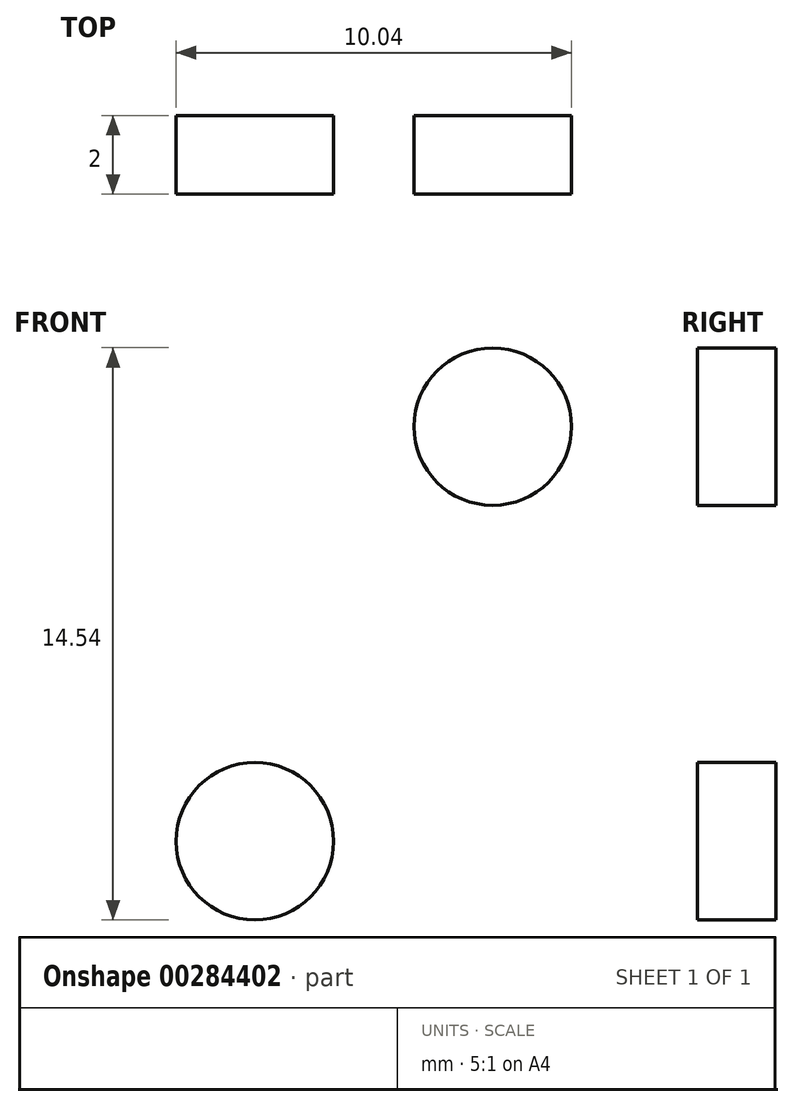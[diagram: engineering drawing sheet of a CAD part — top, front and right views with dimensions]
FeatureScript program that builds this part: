
annotation { "Feature Type Name" : "Feature", "Feature Type Description" : "" }
export const myFeature = defineFeature(function(context is Context, id is Id, definition is map)
    precondition{}
    {
        {
            var Q0;
            Q0=qCreatedBy(makeId("Front.planeOp"),FACE);
            var sketch = newSketch(context, id + "F0", { "sketchPlane" : qUnion([Q0])});
            skCircle(sketch, "E0", {"center": v(0, 0) * mm, "radius": 10 * mm});
            skSolve(sketch);
        }
        {
            var Q0;
            Q0=makeQuery(id+"F0.imprint","IMPRINT",FACE,{"disambiguationData":[TD([[makeQuery(id+"F0.imprint","IMPRINT",EDGE,{"derivedFrom":sQuery(id+"F0.wireOp",EDGE,"E0")}),1.0]])]});
            extrude(context, id + "F1", {"entities" : qUnion([Q0]), "depth" : 2 * mm});
        }
        {
            var Q0;
            Q0=makeQuery(id+"F1.opExtrude","CAP_FACE",FACE,{"disambiguationData":[OSD([sQuery(id+"F0.wireOp",EDGE,"E0")])],"isStart":false});
            var sketch = newSketch(context, id + "F2", { "sketchPlane" : qUnion([Q0])});
            skCircle(sketch, "E1", {"center": v(0, 0) * mm, "radius": 7 * mm});
            skCircle(sketch, "E2", {"center": v(0, 7) * mm, "radius": 2 * mm});
            skCircle(sketch, "E3", {"center": v(6.04, 3.54) * mm, "radius": 2 * mm});
            skCircle(sketch, "E4", {"center": v(5.81, -3.9) * mm, "radius": 2 * mm});
            skCircle(sketch, "E5", {"center": v(0, -7) * mm, "radius": 2 * mm});
            skCircle(sketch, "E6", {"center": v(-6.31, -3.03) * mm, "radius": 2 * mm});
            skCircle(sketch, "E7", {"center": v(-5.68, 4.1) * mm, "radius": 2 * mm});
            skSolve(sketch);
        }
        {
            var Q0;
            {var subQ0=sQuery(id+"F2.wireOp",EDGE,"E7");var subQ1=sQuery(id+"F2.wireOp",EDGE,"E1");var subQ2=makeQuery(id+"F2.imprint","INTERSECT",VERTEX,{"disambiguationData":[OD(0.0)],"derivedFrom":[subQ1,subQ0]});Q0=makeQuery(id+"F2.imprint","IMPRINT",FACE,{"disambiguationData":[TD([[makeQuery(id+"F2.imprint","IMPRINT",EDGE,{"disambiguationData":[TD([[subQ2,-1.0]])],"derivedFrom":subQ1}),-1.0]])]});}
            var Q1;
            {var subQ0=sQuery(id+"F2.wireOp",EDGE,"E7");var subQ1=sQuery(id+"F2.wireOp",EDGE,"E1");var subQ2=makeQuery(id+"F2.imprint","INTERSECT",VERTEX,{"disambiguationData":[OD(0.0)],"derivedFrom":[subQ1,subQ0]});Q1=makeQuery(id+"F2.imprint","IMPRINT",FACE,{"disambiguationData":[TD([[makeQuery(id+"F2.imprint","IMPRINT",EDGE,{"disambiguationData":[TD([[subQ2,-1.0]])],"derivedFrom":subQ1}),1.0]])]});}
            var Q2;
            {var subQ0=sQuery(id+"F2.wireOp",EDGE,"E2");var subQ1=sQuery(id+"F2.wireOp",EDGE,"E1");var subQ2=makeQuery(id+"F2.imprint","INTERSECT",VERTEX,{"disambiguationData":[OD(0.0)],"derivedFrom":[subQ1,subQ0]});Q2=makeQuery(id+"F2.imprint","IMPRINT",FACE,{"disambiguationData":[TD([[makeQuery(id+"F2.imprint","IMPRINT",EDGE,{"disambiguationData":[TD([[subQ2,-1.0]])],"derivedFrom":subQ1}),1.0]])]});}
            var Q3;
            {var subQ0=sQuery(id+"F2.wireOp",EDGE,"E2");var subQ1=sQuery(id+"F2.wireOp",EDGE,"E1");var subQ2=makeQuery(id+"F2.imprint","INTERSECT",VERTEX,{"disambiguationData":[OD(0.0)],"derivedFrom":[subQ1,subQ0]});Q3=makeQuery(id+"F2.imprint","IMPRINT",FACE,{"disambiguationData":[TD([[makeQuery(id+"F2.imprint","IMPRINT",EDGE,{"disambiguationData":[TD([[subQ2,-1.0]])],"derivedFrom":subQ1}),-1.0]])]});}
            var Q4;
            {var subQ0=sQuery(id+"F2.wireOp",EDGE,"E3");var subQ1=sQuery(id+"F2.wireOp",EDGE,"E1");var subQ2=makeQuery(id+"F2.imprint","INTERSECT",VERTEX,{"disambiguationData":[OD(0.0)],"derivedFrom":[subQ1,subQ0]});Q4=makeQuery(id+"F2.imprint","IMPRINT",FACE,{"disambiguationData":[TD([[makeQuery(id+"F2.imprint","IMPRINT",EDGE,{"disambiguationData":[TD([[subQ2,1.0]])],"derivedFrom":subQ1}),-1.0]])]});}
            var Q5;
            {var subQ0=sQuery(id+"F2.wireOp",EDGE,"E3");var subQ1=sQuery(id+"F2.wireOp",EDGE,"E1");var subQ2=makeQuery(id+"F2.imprint","INTERSECT",VERTEX,{"disambiguationData":[OD(0.0)],"derivedFrom":[subQ1,subQ0]});Q5=makeQuery(id+"F2.imprint","IMPRINT",FACE,{"disambiguationData":[TD([[makeQuery(id+"F2.imprint","IMPRINT",EDGE,{"disambiguationData":[TD([[subQ2,1.0]])],"derivedFrom":subQ1}),1.0]])]});}
            var Q6;
            {var subQ0=sQuery(id+"F2.wireOp",EDGE,"E4");var subQ1=sQuery(id+"F2.wireOp",EDGE,"E1");var subQ2=makeQuery(id+"F2.imprint","INTERSECT",VERTEX,{"disambiguationData":[OD(0.0)],"derivedFrom":[subQ1,subQ0]});Q6=makeQuery(id+"F2.imprint","IMPRINT",FACE,{"disambiguationData":[TD([[makeQuery(id+"F2.imprint","IMPRINT",EDGE,{"disambiguationData":[TD([[subQ2,-1.0]])],"derivedFrom":subQ1}),1.0]])]});}
            var Q7;
            {var subQ0=sQuery(id+"F2.wireOp",EDGE,"E4");var subQ1=sQuery(id+"F2.wireOp",EDGE,"E1");var subQ2=makeQuery(id+"F2.imprint","INTERSECT",VERTEX,{"disambiguationData":[OD(0.0)],"derivedFrom":[subQ1,subQ0]});Q7=makeQuery(id+"F2.imprint","IMPRINT",FACE,{"disambiguationData":[TD([[makeQuery(id+"F2.imprint","IMPRINT",EDGE,{"disambiguationData":[TD([[subQ2,-1.0]])],"derivedFrom":subQ1}),-1.0]])]});}
            var Q8;
            {var subQ0=sQuery(id+"F2.wireOp",EDGE,"E5");var subQ1=sQuery(id+"F2.wireOp",EDGE,"E1");var subQ2=makeQuery(id+"F2.imprint","INTERSECT",VERTEX,{"disambiguationData":[OD(0.0)],"derivedFrom":[subQ1,subQ0]});Q8=makeQuery(id+"F2.imprint","IMPRINT",FACE,{"disambiguationData":[TD([[makeQuery(id+"F2.imprint","IMPRINT",EDGE,{"disambiguationData":[TD([[subQ2,-1.0]])],"derivedFrom":subQ1}),-1.0]])]});}
            var Q9;
            {var subQ0=sQuery(id+"F2.wireOp",EDGE,"E5");var subQ1=sQuery(id+"F2.wireOp",EDGE,"E1");var subQ2=makeQuery(id+"F2.imprint","INTERSECT",VERTEX,{"disambiguationData":[OD(0.0)],"derivedFrom":[subQ1,subQ0]});Q9=makeQuery(id+"F2.imprint","IMPRINT",FACE,{"disambiguationData":[TD([[makeQuery(id+"F2.imprint","IMPRINT",EDGE,{"disambiguationData":[TD([[subQ2,-1.0]])],"derivedFrom":subQ1}),1.0]])]});}
            var Q10;
            {var subQ0=sQuery(id+"F2.wireOp",EDGE,"E6");var subQ1=sQuery(id+"F2.wireOp",EDGE,"E1");var subQ2=makeQuery(id+"F2.imprint","INTERSECT",VERTEX,{"disambiguationData":[OD(0.0)],"derivedFrom":[subQ1,subQ0]});Q10=makeQuery(id+"F2.imprint","IMPRINT",FACE,{"disambiguationData":[TD([[makeQuery(id+"F2.imprint","IMPRINT",EDGE,{"disambiguationData":[TD([[subQ2,-1.0]])],"derivedFrom":subQ1}),-1.0]])]});}
            var Q11;
            {var subQ0=sQuery(id+"F2.wireOp",EDGE,"E6");var subQ1=sQuery(id+"F2.wireOp",EDGE,"E1");var subQ2=makeQuery(id+"F2.imprint","INTERSECT",VERTEX,{"disambiguationData":[OD(0.0)],"derivedFrom":[subQ1,subQ0]});Q11=makeQuery(id+"F2.imprint","IMPRINT",FACE,{"disambiguationData":[TD([[makeQuery(id+"F2.imprint","IMPRINT",EDGE,{"disambiguationData":[TD([[subQ2,-1.0]])],"derivedFrom":subQ1}),1.0]])]});}
            extrude(context, id + "F3", {"entities" : qUnion([Q0, Q1, Q2, Q3, Q4, Q5, Q6, Q7, Q8, Q9, Q10, Q11]), "operationType" : NewBodyOperationType.REMOVE, "endBound" : BoundingType.THROUGH_ALL, "oppositeDirection" : true, "depth" : 25.4 * mm});
        }
    });
